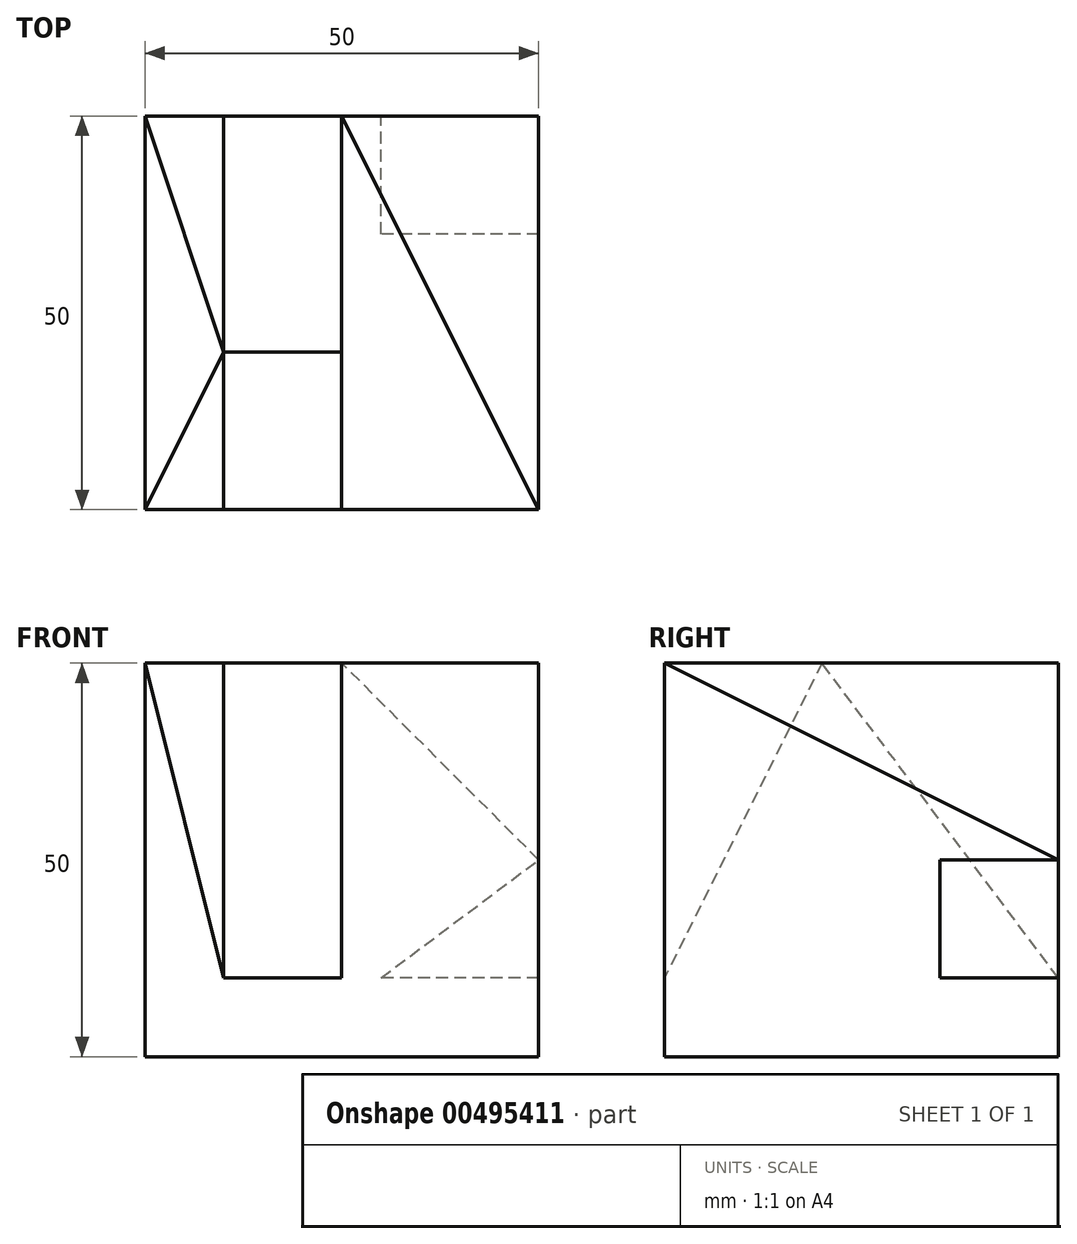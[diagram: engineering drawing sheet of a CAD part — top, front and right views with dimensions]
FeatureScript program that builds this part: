
annotation { "Feature Type Name" : "Feature", "Feature Type Description" : "" }
export const myFeature = defineFeature(function(context is Context, id is Id, definition is map)
    precondition{}
    {
        {
            var Q0;
            Q0=qCreatedBy(makeId("Front.planeOp"),FACE);
            var sketch = newSketch(context, id + "F0", { "sketchPlane" : qUnion([Q0])});
            skLineSegment(sketch, "E0.bottom", {"start": v(0, 0) * mm, "end": v(-50, 0) * mm});
            skLineSegment(sketch, "E0.top", {"start": v(0, 50) * mm, "end": v(-50, 50) * mm});
            skLineSegment(sketch, "E0.left", {"start": v(0, 0) * mm, "end": v(0, 50) * mm});
            skLineSegment(sketch, "E0.right", {"start": v(-50, 0) * mm, "end": v(-50, 50) * mm});
            skSolve(sketch);
        }
        {
            var Q0;
            Q0=makeQuery(id+"F0.imprint","IMPRINT",FACE,{"disambiguationData":[TD([[makeQuery(id+"F0.imprint","IMPRINT",EDGE,{"derivedFrom":sQuery(id+"F0.wireOp",EDGE,"E0.bottom")}),-1.0]])]});
            extrude(context, id + "F1", {"entities" : qUnion([Q0]), "depth" : 50 * mm});
        }
        {
            var Q0;
            Q0=makeQuery(id+"F1.opExtrude","CAP_FACE",FACE,{"disambiguationData":[OSD([sQuery(id+"F0.wireOp",EDGE,"E0.bottom"),sQuery(id+"F0.wireOp",EDGE,"E0.top"),sQuery(id+"F0.wireOp",EDGE,"E0.left"),sQuery(id+"F0.wireOp",EDGE,"E0.right")])],"isStart":true});
            var sketch = newSketch(context, id + "F2", { "sketchPlane" : qUnion([Q0])});
            skLineSegment(sketch, "E1", {"start": v(0, 25) * mm, "end": v(0, 10) * mm});
            skLineSegment(sketch, "E2", {"start": v(0, 10) * mm, "end": v(20, 10) * mm});
            skLineSegment(sketch, "E3", {"start": v(20, 10) * mm, "end": v(0, 25) * mm});
            skSolve(sketch);
        }
        {
            var Q0;
            Q0=makeQuery(id+"F2.imprint","IMPRINT",FACE,{"disambiguationData":[TD([[makeQuery(id+"F2.imprint","IMPRINT",EDGE,{"derivedFrom":sQuery(id+"F2.wireOp",EDGE,"E1")}),-1.0]])]});
            extrude(context, id + "F3", {"entities" : qUnion([Q0]), "operationType" : NewBodyOperationType.REMOVE, "oppositeDirection" : true, "depth" : 15 * mm});
        }
        {
            var Q0;
            Q0=makeQuery(id+"F1.opExtrude","CAP_EDGE",EDGE,{"disambiguationData":[OSD([sQuery(id+"F0.wireOp",EDGE,"E0.top")])],"isStart":true});
            cPoint(context, id + "F4", {"entities" : qUnion([Q0]), "parameter" : 0.5});
        }
        {
            var Q0;
            Q0 = qCreatedBy(id + "F4" ,VERTEX);
            var Q1;
            Q1=makeQuery(id+"F1.opExtrude","CAP_VERTEX",VERTEX,{"disambiguationData":[OSD([sQuery(id+"F0.wireOp",EDGE,"E0.top"),sQuery(id+"F0.wireOp",EDGE,"E0.left")])],"isStart":false});
            var Q2;
            Q2=makeQuery(id+"F3.boolean.opBoolean","COPY",VERTEX,{"derivedFrom":makeQuery(id+"F3.opExtrude","CAP_VERTEX",VERTEX,{"disambiguationData":[OSD([sQuery(id+"F0.wireOp",EDGE,"E0.left"),sQuery(id+"F2.wireOp",EDGE,"E1"),sQuery(id+"F2.wireOp",EDGE,"E3")])],"isStart":true})});
            cPlane(context, id + "F5", {"entities" : qUnion([Q0, Q1, Q2]), "cplaneType" : CPlaneType.THREE_POINT, "offset" : 25 * mm, "width" : 150 * mm, "height" : 150 * mm});
        }
        {
            var Q0;
            Q0=makeQuery(id+"F1.opExtrude","SWEPT_FACE",FACE,{"disambiguationData":[OSD([sQuery(id+"F0.wireOp",EDGE,"E0.top")])]});
            var sketch = newSketch(context, id + "F6", { "sketchPlane" : qUnion([Q0])});
            skLineSegment(sketch, "E4", {"start": v(0, 0) * mm, "end": v(-25, 0) * mm});
            skLineSegment(sketch, "E5", {"start": v(-25, 0) * mm, "end": v(0, -50) * mm});
            skLineSegment(sketch, "E6", {"start": v(0, -50) * mm, "end": v(0, 0) * mm});
            skSolve(sketch);
        }
        {
            var Q0;
            Q0=makeQuery(id+"F6.imprint","IMPRINT",FACE,{"disambiguationData":[TD([[makeQuery(id+"F6.imprint","IMPRINT",EDGE,{"derivedFrom":sQuery(id+"F6.wireOp",EDGE,"E4")}),1.0]])]});
            var Q1;
            Q1=qCreatedBy(id+"F5.planeOp",FACE);
            extrude(context, id + "F7", {"entities" : qUnion([Q0]), "operationType" : NewBodyOperationType.REMOVE, "endBound" : BoundingType.UP_TO_SURFACE, "oppositeDirection" : true, "endBoundEntityFace" : qUnion([Q1]), "depth" : 25 * mm});
        }
        {
            var Q0;
            Q0=makeQuery(id+"F1.opExtrude","CAP_FACE",FACE,{"disambiguationData":[OSD([sQuery(id+"F0.wireOp",EDGE,"E0.bottom"),sQuery(id+"F0.wireOp",EDGE,"E0.top"),sQuery(id+"F0.wireOp",EDGE,"E0.left"),sQuery(id+"F0.wireOp",EDGE,"E0.right")])],"isStart":false});
            var sketch = newSketch(context, id + "F8", { "sketchPlane" : qUnion([Q0])});
            skLineSegment(sketch, "E7.bottom", {"start": v(-40, 50) * mm, "end": v(-25, 50) * mm});
            skLineSegment(sketch, "E7.top", {"start": v(-40, 10) * mm, "end": v(-25, 10) * mm});
            skLineSegment(sketch, "E7.left", {"start": v(-40, 50) * mm, "end": v(-40, 10) * mm});
            skLineSegment(sketch, "E7.right", {"start": v(-25, 50) * mm, "end": v(-25, 10) * mm});
            skSolve(sketch);
        }
        {
            var Q0;
            Q0=makeQuery(id+"F1.opExtrude","SWEPT_FACE",FACE,{"disambiguationData":[OSD([sQuery(id+"F0.wireOp",EDGE,"E0.top")])]});
            var sketch = newSketch(context, id + "F9", { "sketchPlane" : qUnion([Q0])});
            skLineSegment(sketch, "E8.bottom", {"start": v(-25, -50) * mm, "end": v(-40, -50) * mm});
            skLineSegment(sketch, "E8.top", {"start": v(-25, -30) * mm, "end": v(-40, -30) * mm});
            skLineSegment(sketch, "E8.left", {"start": v(-25, -50) * mm, "end": v(-25, -30) * mm});
            skLineSegment(sketch, "E8.right", {"start": v(-40, -50) * mm, "end": v(-40, -30) * mm});
            skSolve(sketch);
        }
        {
            var Q0;
            Q0=sQuery(id+"F9.wireOp",VERTEX,"E8.left.end");
            var Q1;
            Q1=sQuery(id+"F9.wireOp",VERTEX,"E8.bottom.start");
            var Q2;
            Q2=sQuery(id+"F8.wireOp",VERTEX,"E7.right.end");
            cPlane(context, id + "F10", {"entities" : qUnion([Q0, Q1, Q2]), "cplaneType" : CPlaneType.THREE_POINT, "offset" : 25 * mm, "width" : 150 * mm, "height" : 150 * mm});
        }
        {
            var Q0;
            Q0=qCreatedBy(id+"F10.planeOp",FACE);
            var sketch = newSketch(context, id + "F11", { "sketchPlane" : qUnion([Q0])});
            skLineSegment(sketch, "E9", {"start": v(30, 50) * mm, "end": v(50, 10) * mm});
            skSolve(sketch);
        }
        {
            var Q0;
            Q0=makeQuery(id+"F9.imprint","IMPRINT",FACE,{"disambiguationData":[TD([[makeQuery(id+"F9.imprint","IMPRINT",EDGE,{"derivedFrom":sQuery(id+"F9.wireOp",EDGE,"E8.bottom")}),-1.0]])]});
            var Q1;
            Q1=sQuery(id+"F11.wireOp",EDGE,"E9");
            sweep(context, id + "F12", {"operationType" : NewBodyOperationType.REMOVE, "profiles" : qUnion([Q0]), "path" : qUnion([Q1])});
        }
        {
            var Q0;
            Q0=qCreatedBy(id+"F10.planeOp",FACE);
            var sketch = newSketch(context, id + "F13", { "sketchPlane" : qUnion([Q0])});
            skLineSegment(sketch, "E10", {"start": v(30, 50) * mm, "end": v(50, 10) * mm});
            skSolve(sketch);
        }
        {
            var Q0;
            Q0=makeQuery(id+"F1.opExtrude","CAP_FACE",FACE,{"disambiguationData":[OSD([sQuery(id+"F0.wireOp",EDGE,"E0.bottom"),sQuery(id+"F0.wireOp",EDGE,"E0.top"),sQuery(id+"F0.wireOp",EDGE,"E0.left"),sQuery(id+"F0.wireOp",EDGE,"E0.right")])],"isStart":true});
            var sketch = newSketch(context, id + "F14", { "sketchPlane" : qUnion([Q0])});
            skLineSegment(sketch, "E11.bottom", {"start": v(25, 50) * mm, "end": v(40, 50) * mm});
            skLineSegment(sketch, "E11.top", {"start": v(25, 10) * mm, "end": v(40, 10) * mm});
            skLineSegment(sketch, "E11.left", {"start": v(25, 50) * mm, "end": v(25, 10) * mm});
            skLineSegment(sketch, "E11.right", {"start": v(40, 50) * mm, "end": v(40, 10) * mm});
            skSolve(sketch);
        }
        {
            var Q0;
            Q0=qCreatedBy(id+"F10.planeOp",FACE);
            var sketch = newSketch(context, id + "F15", { "sketchPlane" : qUnion([Q0])});
            skLineSegment(sketch, "E12", {"start": v(30, 50) * mm, "end": v(0, 10) * mm});
            skSolve(sketch);
        }
        {
            var Q0;
            Q0=makeQuery(id+"F14.imprint","IMPRINT",FACE,{"disambiguationData":[TD([[makeQuery(id+"F14.imprint","IMPRINT",EDGE,{"derivedFrom":sQuery(id+"F14.wireOp",EDGE,"E11.bottom")}),-1.0]])]});
            var Q1;
            Q1=sQuery(id+"F15.wireOp",EDGE,"E12");
            sweep(context, id + "F16", {"operationType" : NewBodyOperationType.REMOVE, "profiles" : qUnion([Q0]), "path" : qUnion([Q1])});
        }
        {
            var Q0;
            Q0=makeQuery(id+"F1.opExtrude","CAP_VERTEX",VERTEX,{"disambiguationData":[OSD([sQuery(id+"F0.wireOp",EDGE,"E0.top"),sQuery(id+"F0.wireOp",EDGE,"E0.right")])],"isStart":false});
            var Q1;
            Q1=makeQuery(id+"F16.boolean.opBoolean","MERGE",VERTEX,{"derivedFrom":[makeQuery(id+"F12.boolean.opBoolean","COPY",VERTEX,{"derivedFrom":makeQuery(id+"F12.opSweep","CAP_VERTEX",VERTEX,{"disambiguationData":[OSD([sQuery(id+"F9.wireOp",EDGE,"E8.top"),sQuery(id+"F9.wireOp",EDGE,"E8.right"),sQuery(id+"F11.wireOp",EDGE,"E9")])],"isStart":true})}),makeQuery(id+"F16.opSweep","CAP_VERTEX",VERTEX,{"disambiguationData":[OSD([sQuery(id+"F14.wireOp",EDGE,"E11.top"),sQuery(id+"F14.wireOp",EDGE,"E11.right"),sQuery(id+"F15.wireOp",EDGE,"E12")])],"isStart":false})]});
            var Q2;
            Q2=sQuery(id+"F8.wireOp",VERTEX,"E7.left.end");
            cPlane(context, id + "F17", {"entities" : qUnion([Q0, Q1, Q2]), "cplaneType" : CPlaneType.THREE_POINT, "offset" : 25 * mm, "width" : 150 * mm, "height" : 150 * mm});
        }
        {
            var Q0;
            Q0=makeQuery(id+"F12.boolean.opBoolean","COPY",FACE,{"derivedFrom":makeQuery(id+"F12.opSweep","SWEPT_FACE",FACE,{"disambiguationData":[OSD([sQuery(id+"F9.wireOp",EDGE,"E8.right"),sQuery(id+"F11.wireOp",EDGE,"E9")])]})});
            var Q1;
            Q1=qCreatedBy(id+"F17.planeOp",FACE);
            extrude(context, id + "F18", {"entities" : qUnion([Q0]), "operationType" : NewBodyOperationType.REMOVE, "endBound" : BoundingType.UP_TO_SURFACE, "oppositeDirection" : true, "endBoundEntityFace" : qUnion([Q1]), "depth" : 25 * mm});
        }
        {
            var Q0;
            Q0=makeQuery(id+"F16.boolean.opBoolean","COPY",FACE,{"derivedFrom":makeQuery(id+"F16.opSweep","SWEPT_FACE",FACE,{"disambiguationData":[OSD([sQuery(id+"F14.wireOp",EDGE,"E11.right"),sQuery(id+"F15.wireOp",EDGE,"E12")])]})});
            var sketch = newSketch(context, id + "F19", { "sketchPlane" : qUnion([Q0])});
            skLineSegment(sketch, "E13", {"start": v(-30, 50) * mm, "end": v(0, 10) * mm});
            skLineSegment(sketch, "E14", {"start": v(0, 10) * mm, "end": v(0, 50) * mm});
            skLineSegment(sketch, "E15", {"start": v(0, 50) * mm, "end": v(-30, 50) * mm});
            skSolve(sketch);
        }
        {
            var Q0;
            Q0=sQuery(id+"F19.wireOp",VERTEX,"E15.end");
            var Q1;
            Q1=makeQuery(id+"F1.opExtrude","CAP_VERTEX",VERTEX,{"disambiguationData":[OSD([sQuery(id+"F0.wireOp",EDGE,"E0.top"),sQuery(id+"F0.wireOp",EDGE,"E0.right")])],"isStart":true});
            var Q2;
            Q2=sQuery(id+"F19.wireOp",VERTEX,"E14.start");
            cPlane(context, id + "F20", {"entities" : qUnion([Q0, Q1, Q2]), "cplaneType" : CPlaneType.THREE_POINT, "offset" : 25 * mm, "width" : 150 * mm, "height" : 150 * mm});
        }
        {
            var Q0;
            Q0=makeQuery(id+"F19.imprint","IMPRINT",FACE,{"disambiguationData":[TD([[makeQuery(id+"F19.imprint","IMPRINT",EDGE,{"derivedFrom":sQuery(id+"F19.wireOp",EDGE,"E13")}),-1.0]])]});
            var Q1;
            Q1=qCreatedBy(id+"F20.planeOp",FACE);
            extrude(context, id + "F21", {"entities" : qUnion([Q0]), "operationType" : NewBodyOperationType.REMOVE, "endBound" : BoundingType.UP_TO_SURFACE, "oppositeDirection" : true, "endBoundEntityFace" : qUnion([Q1]), "depth" : 25 * mm});
        }
    });
